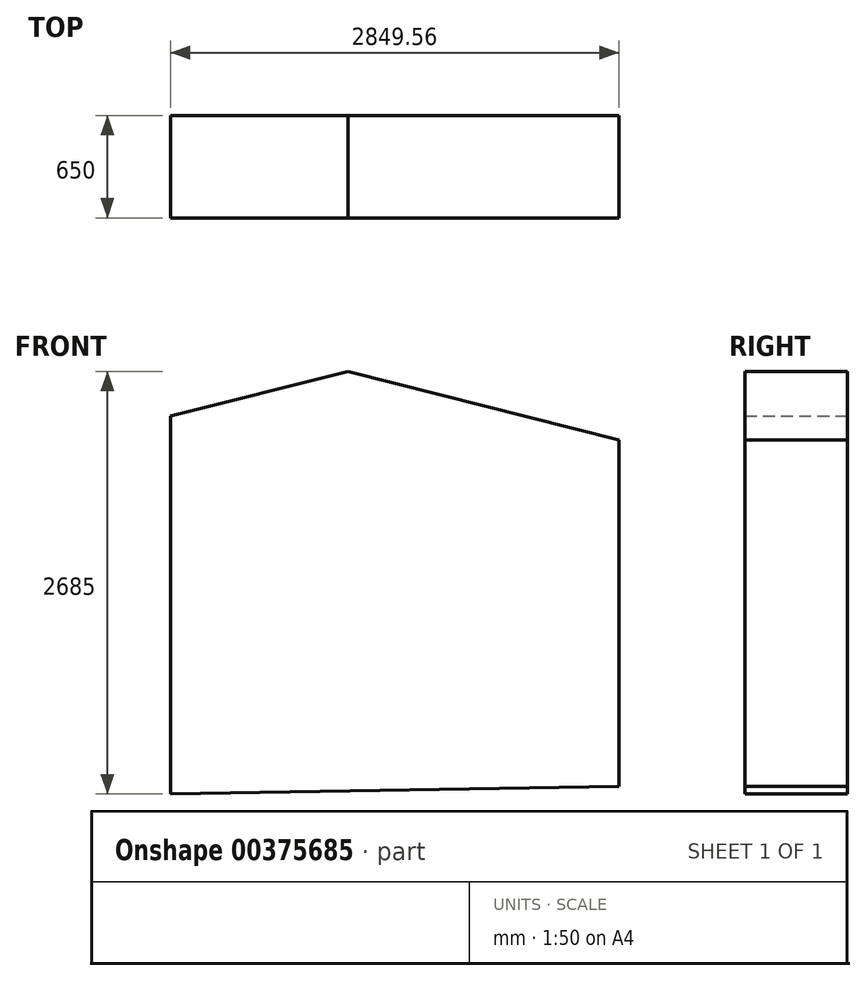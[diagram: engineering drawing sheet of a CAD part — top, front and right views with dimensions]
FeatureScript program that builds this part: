
annotation { "Feature Type Name" : "Feature", "Feature Type Description" : "" }
export const myFeature = defineFeature(function(context is Context, id is Id, definition is map)
    precondition{}
    {
        {
            var Q0;
            Q0=qCreatedBy(makeId("Front.planeOp"),FACE);
            var sketch = newSketch(context, id + "F0", { "sketchPlane" : qUnion([Q0])});
            skLineSegment(sketch, "E0.top", {"start": v(-1424.78, -1200) * mm, "end": v(1424.78, -1150) * mm});
            skLineSegment(sketch, "E0.left", {"start": v(-1424.78, 1200) * mm, "end": v(-1424.78, -1200) * mm});
            skLineSegment(sketch, "E0.right", {"start": v(1424.78, 905) * mm, "end": v(1424.78, -1150) * mm});
            skLineSegment(sketch, "E1", {"start": v(-1424.78, 1200) * mm, "end": v(-296.83, 1485) * mm});
            skLineSegment(sketch, "E2", {"start": v(1424.78, 905) * mm, "end": v(-1424.78, 905) * mm, "construction": true});
            skLineSegment(sketch, "E3", {"start": v(-296.83, 1485) * mm, "end": v(1424.78, 1050) * mm});
            skLineSegment(sketch, "E4", {"start": v(1424.78, 1050) * mm, "end": v(1424.78, 905) * mm});
            skLineSegment(sketch, "E5", {"start": v(-1424.78, 1485) * mm, "end": v(831.12, 1485) * mm, "construction": true});
            skLineSegment(sketch, "E6", {"start": v(-1424.78, 1485) * mm, "end": v(-1424.78, 1200) * mm, "construction": true});
            skLineSegment(sketch, "E7", {"start": v(-1424.78, 0) * mm, "end": v(0, 0) * mm, "construction": true});
            skLineSegment(sketch, "E8", {"start": v(0, 0) * mm, "end": v(0, 905) * mm, "construction": true});
            skLineSegment(sketch, "E9", {"start": v(831.12, 1485) * mm, "end": v(831.12, 1200) * mm, "construction": true});
            skSolve(sketch);
        }
        {
            var Q0;
            Q0 = qSketchRegion(id + "F0", true);
            extrude(context, id + "F1", {"entities" : qUnion([Q0]), "depth" : 650 * mm});
        }
    });
